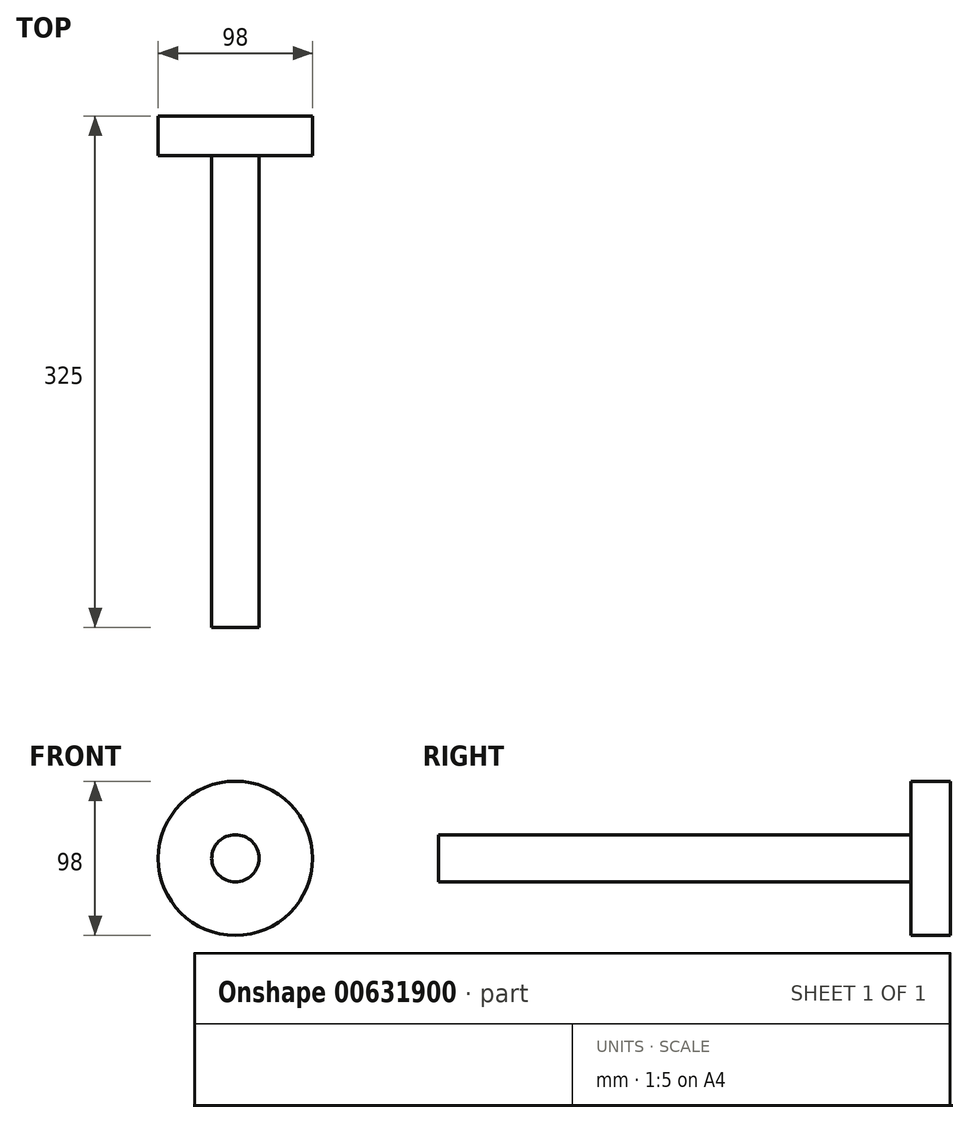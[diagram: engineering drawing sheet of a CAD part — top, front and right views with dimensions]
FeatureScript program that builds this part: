
annotation { "Feature Type Name" : "Feature", "Feature Type Description" : "" }
export const myFeature = defineFeature(function(context is Context, id is Id, definition is map)
    precondition{}
    {
        {
            var Q0;
            Q0=qCreatedBy(makeId("Front.planeOp"),FACE);
            var sketch = newSketch(context, id + "F0", { "sketchPlane" : qUnion([Q0])});
            skCircle(sketch, "E0", {"center": v(-50.17, 23) * mm, "radius": 50 * mm});
            skCircle(sketch, "E1", {"center": v(-50.17, 23) * mm, "radius": 15 * mm});
            skSolve(sketch);
        }
        {
            var Q0;
            Q0=makeQuery(id+"F0.imprint","IMPRINT",FACE,{"disambiguationData":[TD([[makeQuery(id+"F0.imprint","IMPRINT",EDGE,{"derivedFrom":sQuery(id+"F0.wireOp",EDGE,"E1")}),1.0]])]});
            extrude(context, id + "F1", {"entities" : qUnion([Q0]), "depth" : 300 * mm, "offsetDistance" : 25 * mm});
        }
        {
            var Q0;
            Q0=makeQuery(id+"F1.opExtrude","CAP_FACE",FACE,{"disambiguationData":[OSD([sQuery(id+"F0.wireOp",EDGE,"E1")])],"isStart":true});
            var sketch = newSketch(context, id + "F2", { "sketchPlane" : qUnion([Q0])});
            skCircle(sketch, "E2", {"center": v(50.17, 23) * mm, "radius": 49 * mm});
            skSolve(sketch);
        }
        {
            var Q0;
            Q0=makeQuery(id+"F2.imprint","IMPRINT",FACE,{"disambiguationData":[TD([[makeQuery(id+"F2.imprint","IMPRINT",EDGE,{"derivedFrom":sQuery(id+"F2.wireOp",EDGE,"E2")}),1.0]])]});
            var Q1;
            Q1=makeQuery(id+"F2.imprint","IMPRINT",FACE,{"disambiguationData":[TD([[makeQuery(id+"F2.imprint","IMPRINT",EDGE,{"derivedFrom":makeQuery(id+"F1.opExtrude","CAP_EDGE",EDGE,{"disambiguationData":[OSD([sQuery(id+"F0.wireOp",EDGE,"E1")])],"isStart":true})}),-1.0]])]});
            extrude(context, id + "F3", {"entities" : qUnion([Q0, Q1]), "operationType" : NewBodyOperationType.ADD, "depth" : 25 * mm, "offsetDistance" : 25 * mm});
        }
    });
